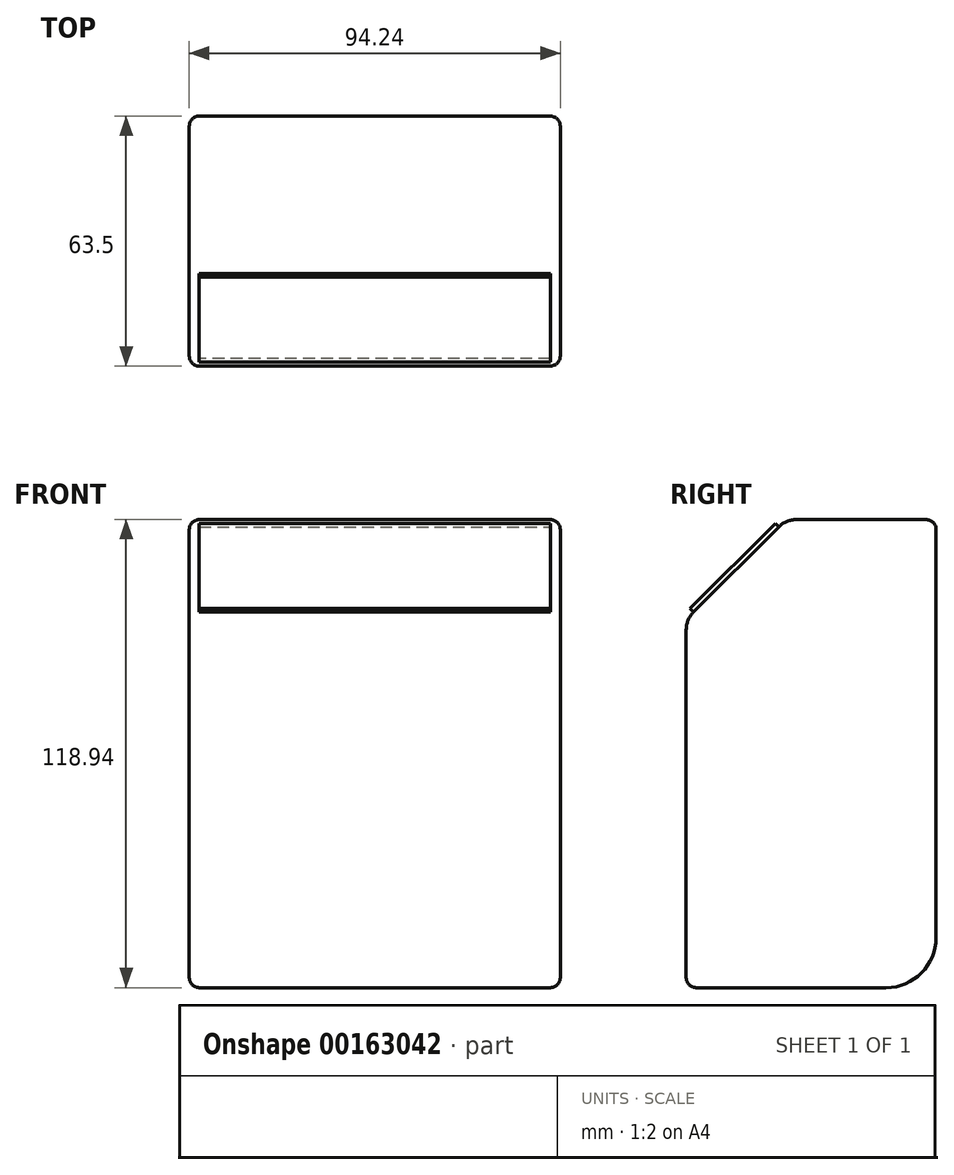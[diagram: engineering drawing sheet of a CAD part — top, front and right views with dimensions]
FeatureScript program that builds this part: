
annotation { "Feature Type Name" : "Feature", "Feature Type Description" : "" }
export const myFeature = defineFeature(function(context is Context, id is Id, definition is map)
    precondition{}
    {
        {
            var Q0;
            Q0=qCreatedBy(makeId("Front.planeOp"),FACE);
            var sketch = newSketch(context, id + "F0", { "sketchPlane" : qUnion([Q0])});
            skLineSegment(sketch, "E0.bottom", {"start": v(48.44, 59.47) * mm, "end": v(-45.8, 59.47) * mm});
            skLineSegment(sketch, "E0.top", {"start": v(48.44, -59.47) * mm, "end": v(-45.8, -59.47) * mm});
            skLineSegment(sketch, "E0.left", {"start": v(48.44, 59.47) * mm, "end": v(48.44, -59.47) * mm});
            skLineSegment(sketch, "E0.right", {"start": v(-45.8, 59.47) * mm, "end": v(-45.8, -59.47) * mm});
            skPoint(sketch, "E0.middle", {"position": v(1.32, 0) * mm});
            skSolve(sketch);
        }
        {
            var Q0;
            Q0=makeQuery(id+"F0.imprint","IMPRINT",FACE,{"disambiguationData":[TD([[makeQuery(id+"F0.imprint","IMPRINT",EDGE,{"derivedFrom":sQuery(id+"F0.wireOp",EDGE,"E0.bottom")}),1.0]])]});
            extrude(context, id + "F1", {"entities" : qUnion([Q0]), "depth" : 63.5 * mm});
        }
        {
            var Q0;
            Q0=makeQuery(id+"F1.opExtrude","CAP_EDGE",EDGE,{"disambiguationData":[OSD([sQuery(id+"F0.wireOp",EDGE,"E0.bottom")])],"isStart":false});
            chamfer(context, id + "F2", {"entities" : qUnion([Q0]), "width" : 25.4 * mm, "tangentPropagation" : true});
        }
        {
            var Q0;
            {var subQ0=sQuery(id+"F0.wireOp",EDGE,"E0.bottom");Q0=makeQuery(id+"F2.opChamfer","BLEND_EDGE",EDGE,{"blendedFrom":[makeQuery(id+"F1.opExtrude","CAP_EDGE",EDGE,{"disambiguationData":[OSD([subQ0])],"isStart":false}),makeQuery(id+"F1.opExtrude","CAP_FACE",FACE,{"disambiguationData":[OSD([subQ0,sQuery(id+"F0.wireOp",EDGE,"E0.top"),sQuery(id+"F0.wireOp",EDGE,"E0.left"),sQuery(id+"F0.wireOp",EDGE,"E0.right")])],"isStart":false})],"blendedInto":[makeQuery(id+"F1.opExtrude","CAP_FACE",FACE,{"disambiguationData":[OSD([subQ0,sQuery(id+"F0.wireOp",EDGE,"E0.top"),sQuery(id+"F0.wireOp",EDGE,"E0.left"),sQuery(id+"F0.wireOp",EDGE,"E0.right")])],"isStart":false})]});}
            var Q1;
            {var subQ0=sQuery(id+"F0.wireOp",EDGE,"E0.bottom");Q1=makeQuery(id+"F2.opChamfer","BLEND_EDGE",EDGE,{"blendedFrom":[makeQuery(id+"F1.opExtrude","CAP_EDGE",EDGE,{"disambiguationData":[OSD([subQ0])],"isStart":false}),makeQuery(id+"F1.opExtrude","SWEPT_FACE",FACE,{"disambiguationData":[OSD([subQ0])]})],"blendedInto":[makeQuery(id+"F1.opExtrude","SWEPT_FACE",FACE,{"disambiguationData":[OSD([subQ0])]})]});}
            fillet(context, id + "F3", {"entities" : qUnion([Q0, Q1]), "radius" : 6.35 * mm, "tangentPropagation" : true, "allowEdgeOverflow" : false});
        }
        {
            var Q0;
            Q0=makeQuery(id+"F1.opExtrude","SWEPT_EDGE",EDGE,{"disambiguationData":[OSD([sQuery(id+"F0.wireOp",EDGE,"E0.bottom"),sQuery(id+"F0.wireOp",EDGE,"E0.right")])]});
            var Q1;
            Q1=makeQuery(id+"F2.opChamfer","BLEND_EDGE",EDGE,{"blendedFrom":[makeQuery(id+"F1.opExtrude","CAP_EDGE",EDGE,{"disambiguationData":[OSD([sQuery(id+"F0.wireOp",EDGE,"E0.bottom")])],"isStart":false}),makeQuery(id+"F1.opExtrude","SWEPT_FACE",FACE,{"disambiguationData":[OSD([sQuery(id+"F0.wireOp",EDGE,"E0.right")])]})],"blendedInto":[makeQuery(id+"F1.opExtrude","SWEPT_FACE",FACE,{"disambiguationData":[OSD([sQuery(id+"F0.wireOp",EDGE,"E0.right")])]})]});
            var Q2;
            Q2=makeQuery(id+"F1.opExtrude","CAP_EDGE",EDGE,{"disambiguationData":[OSD([sQuery(id+"F0.wireOp",EDGE,"E0.right")])],"isStart":false});
            var Q3;
            {var subQ0=sQuery(id+"F0.wireOp",EDGE,"E0.right");var subQ1=sQuery(id+"F0.wireOp",EDGE,"E0.bottom");Q3=makeQuery(id+"F3.opFillet","BLEND_EDGE",EDGE,{"blendedFrom":[makeQuery(id+"F2.opChamfer","BLEND_EDGE",EDGE,{"blendedFrom":[makeQuery(id+"F1.opExtrude","CAP_EDGE",EDGE,{"disambiguationData":[OSD([subQ1])],"isStart":false}),makeQuery(id+"F1.opExtrude","CAP_FACE",FACE,{"disambiguationData":[OSD([subQ1,sQuery(id+"F0.wireOp",EDGE,"E0.top"),sQuery(id+"F0.wireOp",EDGE,"E0.left"),subQ0])],"isStart":false})],"blendedInto":[makeQuery(id+"F1.opExtrude","CAP_FACE",FACE,{"disambiguationData":[OSD([subQ1,sQuery(id+"F0.wireOp",EDGE,"E0.top"),sQuery(id+"F0.wireOp",EDGE,"E0.left"),subQ0])],"isStart":false})]}),makeQuery(id+"F1.opExtrude","SWEPT_FACE",FACE,{"disambiguationData":[OSD([subQ0])]})],"blendedInto":[makeQuery(id+"F1.opExtrude","SWEPT_FACE",FACE,{"disambiguationData":[OSD([subQ0])]})]});}
            var Q4;
            {var subQ0=sQuery(id+"F0.wireOp",EDGE,"E0.bottom");Q4=makeQuery(id+"F3.opFillet","BLEND_EDGE",EDGE,{"blendedFrom":[makeQuery(id+"F2.opChamfer","BLEND_EDGE",EDGE,{"blendedFrom":[makeQuery(id+"F1.opExtrude","CAP_EDGE",EDGE,{"disambiguationData":[OSD([subQ0])],"isStart":false}),makeQuery(id+"F1.opExtrude","SWEPT_FACE",FACE,{"disambiguationData":[OSD([subQ0])]})],"blendedInto":[makeQuery(id+"F1.opExtrude","SWEPT_FACE",FACE,{"disambiguationData":[OSD([subQ0])]})]}),makeQuery(id+"F1.opExtrude","SWEPT_FACE",FACE,{"disambiguationData":[OSD([sQuery(id+"F0.wireOp",EDGE,"E0.right")])]})],"blendedInto":[makeQuery(id+"F1.opExtrude","SWEPT_FACE",FACE,{"disambiguationData":[OSD([sQuery(id+"F0.wireOp",EDGE,"E0.right")])]})]});}
            var Q5;
            Q5=makeQuery(id+"F1.opExtrude","SWEPT_EDGE",EDGE,{"disambiguationData":[OSD([sQuery(id+"F0.wireOp",EDGE,"E0.bottom"),sQuery(id+"F0.wireOp",EDGE,"E0.left")])]});
            var Q6;
            {var subQ0=sQuery(id+"F0.wireOp",EDGE,"E0.bottom");Q6=makeQuery(id+"F3.opFillet","BLEND_EDGE",EDGE,{"blendedFrom":[makeQuery(id+"F2.opChamfer","BLEND_EDGE",EDGE,{"blendedFrom":[makeQuery(id+"F1.opExtrude","CAP_EDGE",EDGE,{"disambiguationData":[OSD([subQ0])],"isStart":false}),makeQuery(id+"F1.opExtrude","SWEPT_FACE",FACE,{"disambiguationData":[OSD([subQ0])]})],"blendedInto":[makeQuery(id+"F1.opExtrude","SWEPT_FACE",FACE,{"disambiguationData":[OSD([subQ0])]})]}),makeQuery(id+"F1.opExtrude","SWEPT_FACE",FACE,{"disambiguationData":[OSD([sQuery(id+"F0.wireOp",EDGE,"E0.left")])]})],"blendedInto":[makeQuery(id+"F1.opExtrude","SWEPT_FACE",FACE,{"disambiguationData":[OSD([sQuery(id+"F0.wireOp",EDGE,"E0.left")])]})]});}
            var Q7;
            Q7=makeQuery(id+"F2.opChamfer","BLEND_EDGE",EDGE,{"blendedFrom":[makeQuery(id+"F1.opExtrude","CAP_EDGE",EDGE,{"disambiguationData":[OSD([sQuery(id+"F0.wireOp",EDGE,"E0.bottom")])],"isStart":false}),makeQuery(id+"F1.opExtrude","SWEPT_FACE",FACE,{"disambiguationData":[OSD([sQuery(id+"F0.wireOp",EDGE,"E0.left")])]})],"blendedInto":[makeQuery(id+"F1.opExtrude","SWEPT_FACE",FACE,{"disambiguationData":[OSD([sQuery(id+"F0.wireOp",EDGE,"E0.left")])]})]});
            var Q8;
            {var subQ0=sQuery(id+"F0.wireOp",EDGE,"E0.left");var subQ1=sQuery(id+"F0.wireOp",EDGE,"E0.bottom");Q8=makeQuery(id+"F3.opFillet","BLEND_EDGE",EDGE,{"blendedFrom":[makeQuery(id+"F2.opChamfer","BLEND_EDGE",EDGE,{"blendedFrom":[makeQuery(id+"F1.opExtrude","CAP_EDGE",EDGE,{"disambiguationData":[OSD([subQ1])],"isStart":false}),makeQuery(id+"F1.opExtrude","CAP_FACE",FACE,{"disambiguationData":[OSD([subQ1,sQuery(id+"F0.wireOp",EDGE,"E0.top"),subQ0,sQuery(id+"F0.wireOp",EDGE,"E0.right")])],"isStart":false})],"blendedInto":[makeQuery(id+"F1.opExtrude","CAP_FACE",FACE,{"disambiguationData":[OSD([subQ1,sQuery(id+"F0.wireOp",EDGE,"E0.top"),subQ0,sQuery(id+"F0.wireOp",EDGE,"E0.right")])],"isStart":false})]}),makeQuery(id+"F1.opExtrude","SWEPT_FACE",FACE,{"disambiguationData":[OSD([subQ0])]})],"blendedInto":[makeQuery(id+"F1.opExtrude","SWEPT_FACE",FACE,{"disambiguationData":[OSD([subQ0])]})]});}
            var Q9;
            Q9=makeQuery(id+"F1.opExtrude","CAP_EDGE",EDGE,{"disambiguationData":[OSD([sQuery(id+"F0.wireOp",EDGE,"E0.left")])],"isStart":false});
            fillet(context, id + "F4", {"entities" : qUnion([Q0, Q1, Q2, Q3, Q4, Q5, Q6, Q7, Q8, Q9]), "radius" : 2.54 * mm, "tangentPropagation" : true, "allowEdgeOverflow" : false});
        }
        {
            var Q0;
            Q0=makeQuery(id+"F1.opExtrude","CAP_EDGE",EDGE,{"disambiguationData":[OSD([sQuery(id+"F0.wireOp",EDGE,"E0.top")])],"isStart":true});
            fillet(context, id + "F5", {"entities" : qUnion([Q0]), "radius" : 12.7 * mm, "tangentPropagation" : true, "allowEdgeOverflow" : false});
        }
        {
            var Q0;
            Q0=makeQuery(id+"F1.opExtrude","CAP_EDGE",EDGE,{"disambiguationData":[OSD([sQuery(id+"F0.wireOp",EDGE,"E0.left")])],"isStart":true});
            var Q1;
            Q1=makeQuery(id+"F5.opFillet","BLEND_EDGE",EDGE,{"blendedFrom":[makeQuery(id+"F1.opExtrude","CAP_EDGE",EDGE,{"disambiguationData":[OSD([sQuery(id+"F0.wireOp",EDGE,"E0.top")])],"isStart":true}),makeQuery(id+"F1.opExtrude","SWEPT_FACE",FACE,{"disambiguationData":[OSD([sQuery(id+"F0.wireOp",EDGE,"E0.left")])]})],"blendedInto":[makeQuery(id+"F1.opExtrude","SWEPT_FACE",FACE,{"disambiguationData":[OSD([sQuery(id+"F0.wireOp",EDGE,"E0.left")])]})]});
            var Q2;
            Q2=makeQuery(id+"F1.opExtrude","CAP_EDGE",EDGE,{"disambiguationData":[OSD([sQuery(id+"F0.wireOp",EDGE,"E0.right")])],"isStart":true});
            var Q3;
            Q3=makeQuery(id+"F5.opFillet","BLEND_EDGE",EDGE,{"blendedFrom":[makeQuery(id+"F1.opExtrude","CAP_EDGE",EDGE,{"disambiguationData":[OSD([sQuery(id+"F0.wireOp",EDGE,"E0.top")])],"isStart":true}),makeQuery(id+"F1.opExtrude","SWEPT_FACE",FACE,{"disambiguationData":[OSD([sQuery(id+"F0.wireOp",EDGE,"E0.right")])]})],"blendedInto":[makeQuery(id+"F1.opExtrude","SWEPT_FACE",FACE,{"disambiguationData":[OSD([sQuery(id+"F0.wireOp",EDGE,"E0.right")])]})]});
            fillet(context, id + "F6", {"entities" : qUnion([Q0, Q1, Q2, Q3]), "radius" : 2.54 * mm, "tangentPropagation" : true, "allowEdgeOverflow" : false});
        }
        {
            var Q0;
            Q0=makeQuery(id+"F2.opChamfer","BLEND_FACE",FACE,{"disambiguationData":[OSD([sQuery(id+"F0.wireOp",EDGE,"E0.bottom")])]});
            var sketch = newSketch(context, id + "F7", { "sketchPlane" : qUnion([Q0])});
            skLineSegment(sketch, "E1.bottom", {"start": v(-43.26, -18.18) * mm, "end": v(45.9, -18.18) * mm});
            skLineSegment(sketch, "E1.top", {"start": v(-43.26, 12.48) * mm, "end": v(45.9, 12.48) * mm});
            skLineSegment(sketch, "E1.left", {"start": v(-43.26, -18.18) * mm, "end": v(-43.26, 12.48) * mm});
            skLineSegment(sketch, "E1.right", {"start": v(45.9, -18.18) * mm, "end": v(45.9, 12.48) * mm});
            skSolve(sketch);
        }
        {
            var Q0;
            Q0=makeQuery(id+"F7.imprint","IMPRINT",FACE,{"disambiguationData":[TD([[makeQuery(id+"F7.imprint","IMPRINT",EDGE,{"derivedFrom":sQuery(id+"F7.wireOp",EDGE,"E1.bottom")}),1.0]])]});
            extrude(context, id + "F8", {"entities" : qUnion([Q0]), "operationType" : NewBodyOperationType.ADD, "depth" : 1.27 * mm});
        }
    });
